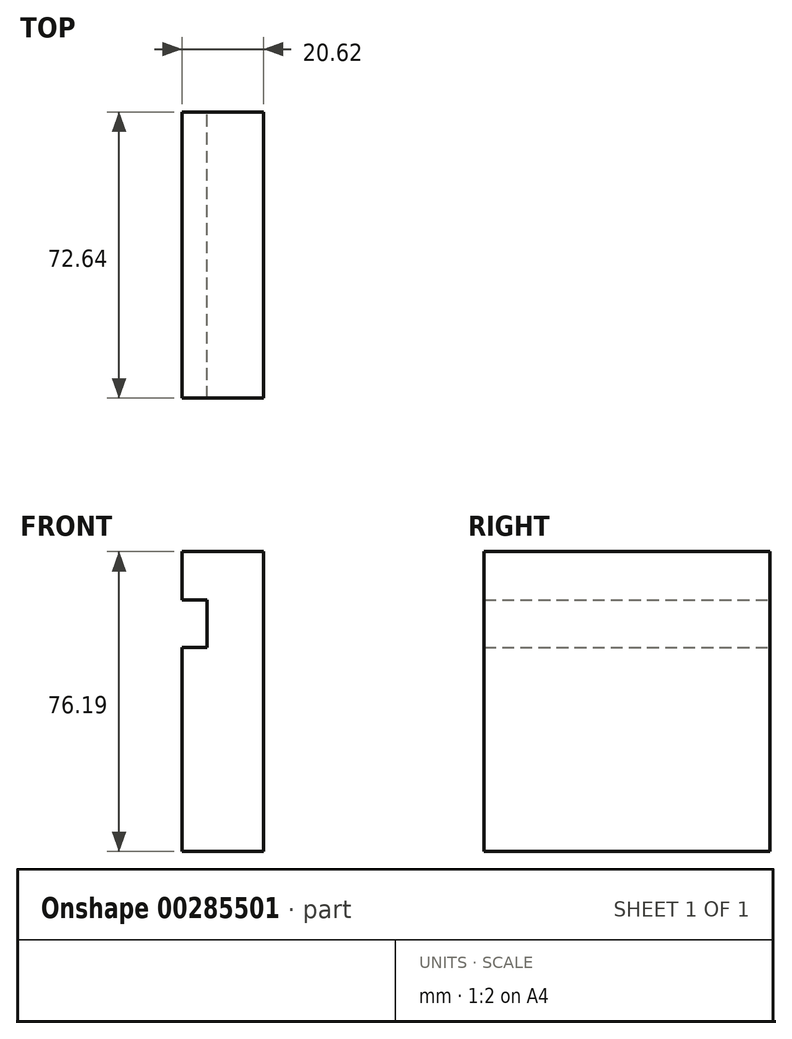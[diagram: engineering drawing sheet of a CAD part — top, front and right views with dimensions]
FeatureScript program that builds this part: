
annotation { "Feature Type Name" : "Feature", "Feature Type Description" : "" }
export const myFeature = defineFeature(function(context is Context, id is Id, definition is map)
    precondition{}
    {
        {
            var Q0;
            Q0=qCreatedBy(makeId("Front.planeOp"),FACE);
            var sketch = newSketch(context, id + "F0", { "sketchPlane" : qUnion([Q0])});
            skLineSegment(sketch, "E0.bottom", {"start": v(0, 0) * mm, "end": v(-20.62, 0) * mm});
            skLineSegment(sketch, "E0.top", {"start": v(0, 76.2) * mm, "end": v(-20.62, 76.2) * mm});
            skLineSegment(sketch, "E0.left", {"start": v(0, 0) * mm, "end": v(0, 76.2) * mm});
            skLineSegment(sketch, "E0.right", {"start": v(-20.62, 0) * mm, "end": v(-20.62, 51.83) * mm});
            skLineSegment(sketch, "E1.bottom", {"start": v(-20.62, 63.9) * mm, "end": v(-14.27, 63.9) * mm});
            skLineSegment(sketch, "E1.top", {"start": v(-20.62, 51.83) * mm, "end": v(-14.27, 51.83) * mm});
            skLineSegment(sketch, "E1.right", {"start": v(-14.27, 63.9) * mm, "end": v(-14.27, 51.83) * mm});
            skLineSegment(sketch, "E2.trimOffspring", {"start": v(-20.62, 63.9) * mm, "end": v(-20.62, 76.2) * mm});
            skSolve(sketch);
        }
        {
            var Q0;
            Q0=qSketchRegion(id+"F0",true);
            extrude(context, id + "F1", {"entities" : qUnion([Q0]), "depth" : 72.64 * mm});
        }
    });
